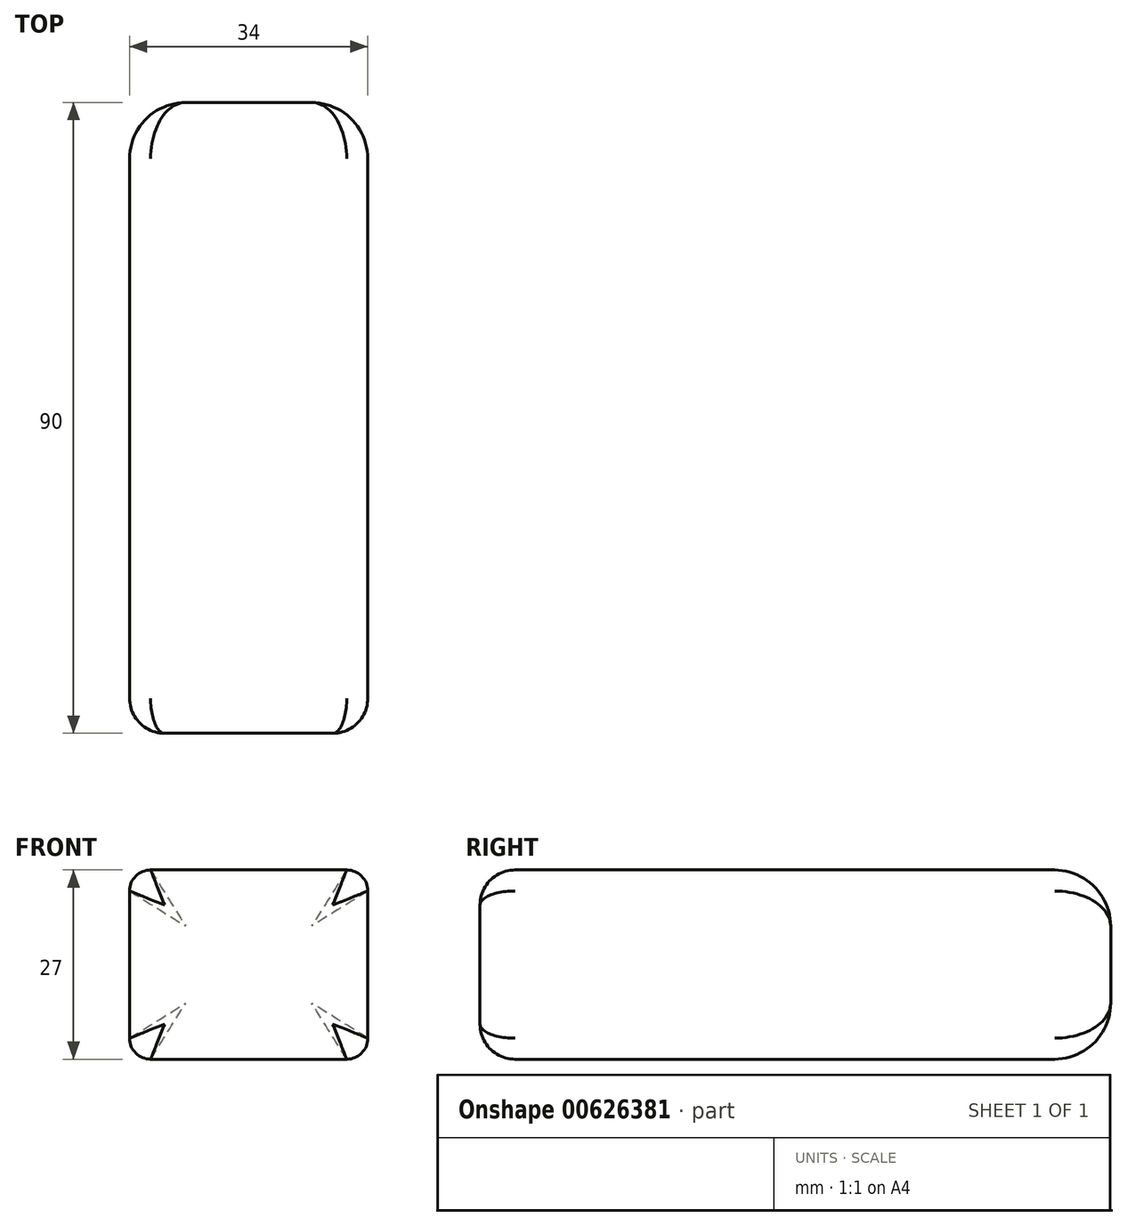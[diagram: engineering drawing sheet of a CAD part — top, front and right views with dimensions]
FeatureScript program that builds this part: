
annotation { "Feature Type Name" : "Feature", "Feature Type Description" : "" }
export const myFeature = defineFeature(function(context is Context, id is Id, definition is map)
    precondition{}
    {
        {
            var Q0;
            Q0=qCreatedBy(makeId("Top.planeOp"),FACE);
            var sketch = newSketch(context, id + "F0", { "sketchPlane" : qUnion([Q0])});
            skLineSegment(sketch, "E0.bottom", {"start": v(-17, 45) * mm, "end": v(17, 45) * mm});
            skLineSegment(sketch, "E0.top", {"start": v(-17, -45) * mm, "end": v(17, -45) * mm});
            skLineSegment(sketch, "E0.left", {"start": v(-17, 45) * mm, "end": v(-17, -45) * mm});
            skLineSegment(sketch, "E0.right", {"start": v(17, 45) * mm, "end": v(17, -45) * mm});
            skPoint(sketch, "E0.middle", {"position": v(0, 0) * mm});
            skSolve(sketch);
        }
        {
            var Q0;
            Q0=makeQuery(id+"F0.imprint","IMPRINT",FACE,{"disambiguationData":[TD([[makeQuery(id+"F0.imprint","IMPRINT",EDGE,{"derivedFrom":sQuery(id+"F0.wireOp",EDGE,"E0.bottom")}),-1.0]])]});
            extrude(context, id + "F1", {"entities" : qUnion([Q0]), "depth" : 27 * mm, "offsetDistance" : 25 * mm});
        }
        {
            var Q0;
            Q0=makeQuery(id+"F1.opExtrude","CAP_EDGE",EDGE,{"disambiguationData":[OSD([sQuery(id+"F0.wireOp",EDGE,"E0.top")])],"isStart":false});
            var Q1;
            Q1=makeQuery(id+"F1.opExtrude","CAP_EDGE",EDGE,{"disambiguationData":[OSD([sQuery(id+"F0.wireOp",EDGE,"E0.top")])],"isStart":true});
            var Q2;
            Q2=makeQuery(id+"F1.opExtrude","SWEPT_EDGE",EDGE,{"disambiguationData":[OSD([sQuery(id+"F0.wireOp",EDGE,"E0.top"),sQuery(id+"F0.wireOp",EDGE,"E0.right")])]});
            var Q3;
            Q3=makeQuery(id+"F1.opExtrude","SWEPT_EDGE",EDGE,{"disambiguationData":[OSD([sQuery(id+"F0.wireOp",EDGE,"E0.top"),sQuery(id+"F0.wireOp",EDGE,"E0.left")])]});
            fillet(context, id + "F2", {"entities" : qUnion([Q0, Q1, Q2, Q3]), "radius" : 5 * mm, "tangentPropagation" : true, "allowEdgeOverflow" : false});
        }
        {
            var Q0;
            Q0=makeQuery(id+"F1.opExtrude","CAP_EDGE",EDGE,{"disambiguationData":[OSD([sQuery(id+"F0.wireOp",EDGE,"E0.left")])],"isStart":false});
            var Q1;
            Q1=makeQuery(id+"F1.opExtrude","CAP_EDGE",EDGE,{"disambiguationData":[OSD([sQuery(id+"F0.wireOp",EDGE,"E0.right")])],"isStart":false});
            var Q2;
            Q2=makeQuery(id+"F1.opExtrude","CAP_EDGE",EDGE,{"disambiguationData":[OSD([sQuery(id+"F0.wireOp",EDGE,"E0.right")])],"isStart":true});
            var Q3;
            Q3=makeQuery(id+"F1.opExtrude","CAP_EDGE",EDGE,{"disambiguationData":[OSD([sQuery(id+"F0.wireOp",EDGE,"E0.left")])],"isStart":true});
            fillet(context, id + "F3", {"entities" : qUnion([Q0, Q1, Q2, Q3]), "radius" : 3 * mm, "tangentPropagation" : true, "allowEdgeOverflow" : false});
        }
        {
            var Q0;
            Q0=makeQuery(id+"F1.opExtrude","CAP_EDGE",EDGE,{"disambiguationData":[OSD([sQuery(id+"F0.wireOp",EDGE,"E0.bottom")])],"isStart":false});
            var Q1;
            Q1=makeQuery(id+"F1.opExtrude","CAP_EDGE",EDGE,{"disambiguationData":[OSD([sQuery(id+"F0.wireOp",EDGE,"E0.bottom")])],"isStart":true});
            fillet(context, id + "F4", {"entities" : qUnion([Q0, Q1]), "radius" : 8 * mm, "tangentPropagation" : true, "allowEdgeOverflow" : false});
        }
    });
